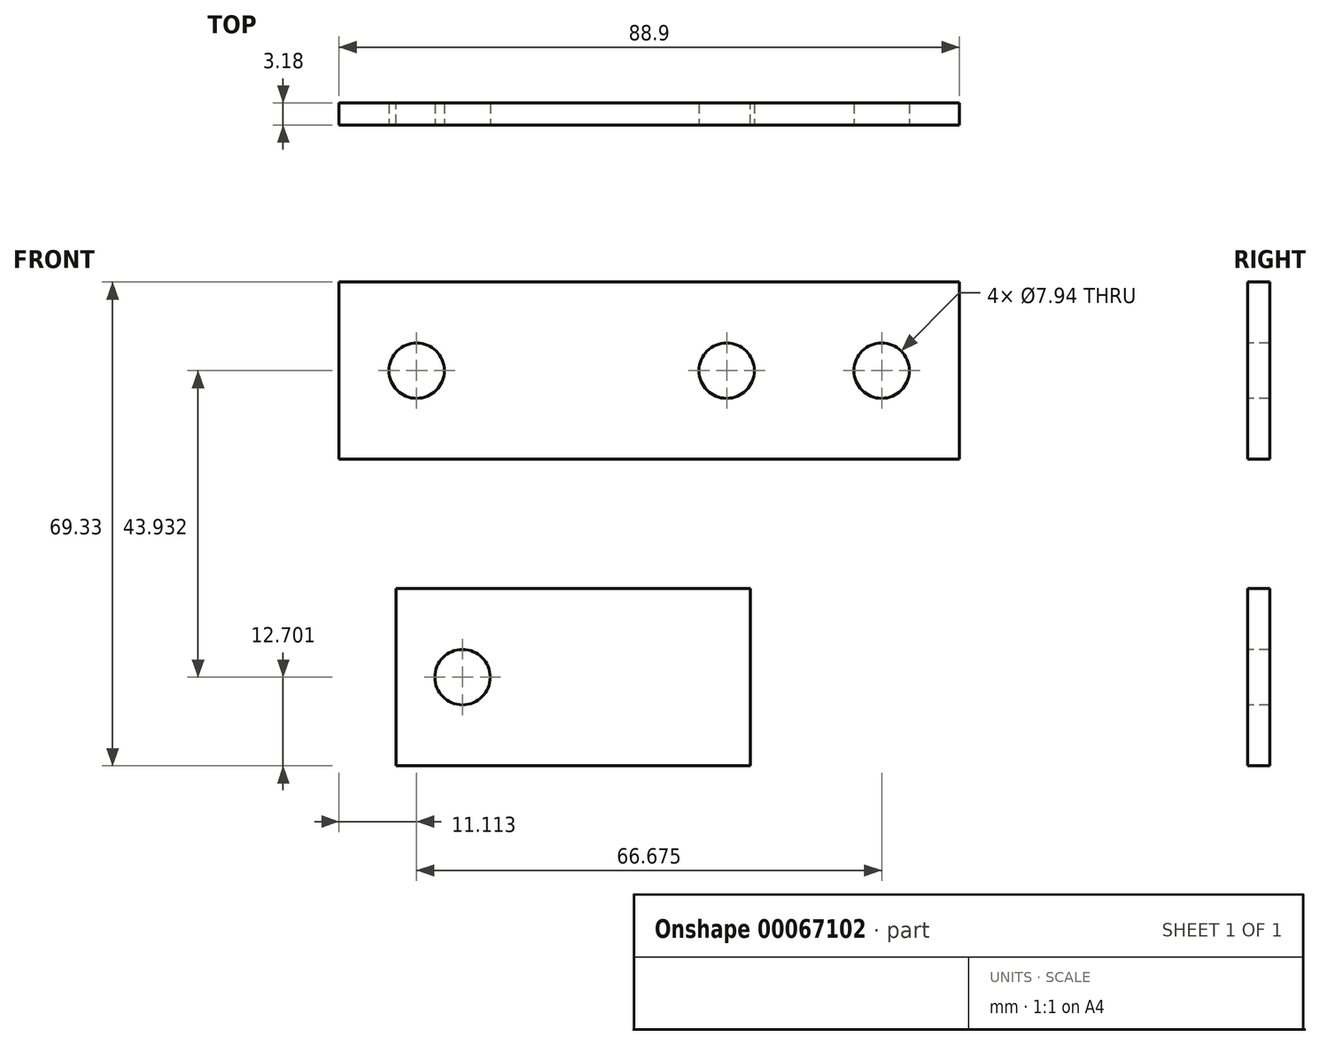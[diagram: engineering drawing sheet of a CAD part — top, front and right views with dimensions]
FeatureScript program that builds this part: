
annotation { "Feature Type Name" : "Feature", "Feature Type Description" : "" }
export const myFeature = defineFeature(function(context is Context, id is Id, definition is map)
    precondition{}
    {
        {
            var Q0;
            Q0=qCreatedBy(makeId("Front.planeOp"),FACE);
            var sketch = newSketch(context, id + "F0", { "sketchPlane" : qUnion([Q0])});
            skLineSegment(sketch, "E0.bottom", {"start": v(-61.5, 59.25) * mm, "end": v(27.4, 59.25) * mm});
            skLineSegment(sketch, "E0.top", {"start": v(-61.5, 33.85) * mm, "end": v(27.4, 33.85) * mm});
            skLineSegment(sketch, "E0.left", {"start": v(-61.5, 59.25) * mm, "end": v(-61.5, 33.85) * mm});
            skLineSegment(sketch, "E0.right", {"start": v(27.4, 59.25) * mm, "end": v(27.4, 33.85) * mm});
            skLineSegment(sketch, "E1.bottom", {"start": v(-53.34, 15.32) * mm, "end": v(-2.54, 15.32) * mm});
            skLineSegment(sketch, "E1.top", {"start": v(-53.34, -10.08) * mm, "end": v(-2.54, -10.08) * mm});
            skLineSegment(sketch, "E1.left", {"start": v(-53.34, 15.32) * mm, "end": v(-53.34, -10.08) * mm});
            skLineSegment(sketch, "E1.right", {"start": v(-2.54, 15.32) * mm, "end": v(-2.54, -10.08) * mm});
            skSolve(sketch);
        }
        {
            var Q0;
            Q0=makeQuery(id+"F0.imprint","IMPRINT",FACE,{"disambiguationData":[TD([[makeQuery(id+"F0.imprint","IMPRINT",EDGE,{"derivedFrom":sQuery(id+"F0.wireOp",EDGE,"E0.bottom")}),-1.0]])]});
            var Q1;
            Q1=makeQuery(id+"F0.imprint","IMPRINT",FACE,{"disambiguationData":[TD([[makeQuery(id+"F0.imprint","IMPRINT",EDGE,{"derivedFrom":sQuery(id+"F0.wireOp",EDGE,"E1.bottom")}),-1.0]])]});
            extrude(context, id + "F1", {"entities" : qUnion([Q0, Q1]), "depth" : 3.17 * mm});
        }
        {
            var Q0;
            Q0=makeQuery(id+"F1.opExtrude","CAP_FACE",FACE,{"disambiguationData":[OSD([sQuery(id+"F0.wireOp",EDGE,"E0.bottom"),sQuery(id+"F0.wireOp",EDGE,"E0.top"),sQuery(id+"F0.wireOp",EDGE,"E0.left"),sQuery(id+"F0.wireOp",EDGE,"E0.right")])],"isStart":false});
            var sketch = newSketch(context, id + "F2", { "sketchPlane" : qUnion([Q0])});
            skLineSegment(sketch, "E2.0", {"start": v(-61.5, 59.25) * mm, "end": v(27.4, 59.25) * mm});
            skLineSegment(sketch, "E2.1", {"start": v(-61.5, 59.25) * mm, "end": v(-61.5, 33.85) * mm});
            skLineSegment(sketch, "E2.2", {"start": v(-61.5, 33.85) * mm, "end": v(27.4, 33.85) * mm});
            skLineSegment(sketch, "E2.3", {"start": v(27.4, 59.25) * mm, "end": v(27.4, 33.85) * mm});
            skLineSegment(sketch, "E3.0", {"start": v(-53.34, 15.32) * mm, "end": v(-53.34, -10.08) * mm});
            skLineSegment(sketch, "E3.1", {"start": v(-53.34, 15.32) * mm, "end": v(-2.54, 15.32) * mm});
            skLineSegment(sketch, "E3.2", {"start": v(-2.54, 15.32) * mm, "end": v(-2.54, -10.08) * mm});
            skLineSegment(sketch, "E3.3", {"start": v(-53.34, -10.08) * mm, "end": v(-2.54, -10.08) * mm});
            skLineSegment(sketch, "E4", {"start": v(-61.5, 59.25) * mm, "end": v(27.4, 33.85) * mm, "construction": true});
            skLineSegment(sketch, "E5", {"start": v(-17.05, 59.25) * mm, "end": v(-17.05, 33.85) * mm, "construction": true});
            skLineSegment(sketch, "E6", {"start": v(-17.05, 59.25) * mm, "end": v(-61.5, 33.85) * mm, "construction": true});
            skLineSegment(sketch, "E7", {"start": v(-2.54, 15.32) * mm, "end": v(-53.34, -10.08) * mm, "construction": true});
            skLineSegment(sketch, "E8", {"start": v(-27.94, 15.32) * mm, "end": v(-27.94, -10.08) * mm, "construction": true});
            skLineSegment(sketch, "E9", {"start": v(-27.94, -10.08) * mm, "end": v(-2.54, -10.08) * mm, "construction": true});
            skLineSegment(sketch, "E10", {"start": v(-27.94, 15.32) * mm, "end": v(-2.54, -10.08) * mm, "construction": true});
            skLineSegment(sketch, "E11", {"start": v(-27.94, 15.32) * mm, "end": v(-53.34, -10.08) * mm, "construction": true});
            skLineSegment(sketch, "E12", {"start": v(-39.27, 59.25) * mm, "end": v(-39.27, 33.85) * mm, "construction": true});
            skPoint(sketch, "E12.startSnap0", {"position": v(-39.27, 46.55) * mm});
            skLineSegment(sketch, "E13", {"start": v(-61.5, 59.25) * mm, "end": v(-39.27, 33.85) * mm, "construction": true});
            skCircle(sketch, "E14", {"center": v(-50.39, 46.55) * mm, "radius": 3.97 * mm});
            skLineSegment(sketch, "E15", {"start": v(-53.34, 2.62) * mm, "end": v(-2.54, 2.62) * mm, "construction": true});
            skCircle(sketch, "E16", {"center": v(-43.81, 2.62) * mm, "radius": 3.97 * mm});
            skLineSegment(sketch, "E17", {"start": v(-17.05, 59.25) * mm, "end": v(27.4, 33.85) * mm, "construction": true});
            skLineSegment(sketch, "E18", {"start": v(5.18, 59.25) * mm, "end": v(5.18, 33.85) * mm, "construction": true});
            skLineSegment(sketch, "E19", {"start": v(-17.05, 59.25) * mm, "end": v(5.18, 33.85) * mm, "construction": true});
            skLineSegment(sketch, "E20", {"start": v(27.4, 59.25) * mm, "end": v(5.18, 33.85) * mm, "construction": true});
            skCircle(sketch, "E21", {"center": v(-5.94, 46.55) * mm, "radius": 3.97 * mm});
            skCircle(sketch, "E22", {"center": v(16.29, 46.55) * mm, "radius": 3.97 * mm});
            skSolve(sketch);
        }
        {
            var Q0;
            Q0=makeQuery(id+"F2.imprint","IMPRINT",FACE,{"disambiguationData":[TD([[makeQuery(id+"F2.imprint","IMPRINT",EDGE,{"derivedFrom":sQuery(id+"F2.wireOp",EDGE,"E14")}),1.0]])]});
            var Q1;
            Q1=makeQuery(id+"F2.imprint","IMPRINT",FACE,{"disambiguationData":[TD([[makeQuery(id+"F2.imprint","IMPRINT",EDGE,{"derivedFrom":sQuery(id+"F2.wireOp",EDGE,"5b00a3e6-2626-47ab-8c37-094255815b48")}),1.0]])]});
            var Q2;
            Q2=makeQuery(id+"F2.imprint","IMPRINT",FACE,{"disambiguationData":[TD([[makeQuery(id+"F2.imprint","IMPRINT",EDGE,{"derivedFrom":sQuery(id+"F2.wireOp",EDGE,"209278f3-97e1-49d9-9f66-f7d8035ce954")}),1.0]])]});
            var Q3;
            Q3=makeQuery(id+"F2.imprint","IMPRINT",FACE,{"disambiguationData":[TD([[makeQuery(id+"F2.imprint","IMPRINT",EDGE,{"derivedFrom":sQuery(id+"F2.wireOp",EDGE,"E16")}),1.0]])]});
            var Q4;
            Q4=makeQuery(id+"F2.imprint","IMPRINT",FACE,{"disambiguationData":[TD([[makeQuery(id+"F2.imprint","IMPRINT",EDGE,{"derivedFrom":sQuery(id+"F2.wireOp",EDGE,"E21")}),1.0]])]});
            var Q5;
            Q5=makeQuery(id+"F2.imprint","IMPRINT",FACE,{"disambiguationData":[TD([[makeQuery(id+"F2.imprint","IMPRINT",EDGE,{"derivedFrom":sQuery(id+"F2.wireOp",EDGE,"E22")}),1.0]])]});
            extrude(context, id + "F3", {"entities" : qUnion([Q0, Q1, Q2, Q3, Q4, Q5]), "operationType" : NewBodyOperationType.REMOVE, "endBound" : BoundingType.THROUGH_ALL, "oppositeDirection" : true, "depth" : 25.4 * mm});
        }
    });
